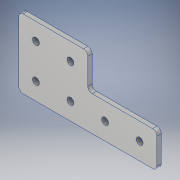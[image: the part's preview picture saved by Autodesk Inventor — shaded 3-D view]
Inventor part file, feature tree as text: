
AUTODESK INVENTOR PART (.ipt)
format: ipt  version: 2018 (Build 220112000, 112)  size: 135,168 bytes
history: native  units: in
note: dims shown in document units (in); Inventor stores cm internally (conversion verified against a paired STEP export)
features: extrude x1, fillet x1, sketch x1
ambient origin geometry x8: Origin, YZ Plane, XZ Plane, XY Plane, X Axis, Y Axis, Z Axis, Center Point
bodies: Solid1 (feature_tree)
feature tree (3):
  extrude  "Extrusion1"  Depth=2.0in
  fillet  "Fillet1"  Radius=1.0in
  sketch  "Sketch1"  dims[d0=2.0in d1=2.0in d2=1.0in d3=2.0in d4=0.5in d5=0.5in d6=1.0in d8=1.0in d9=1.0in d10=2.0in d11=1.0in d12=0.2in d13=0.125in d14=0.0in d15=0.125in]
